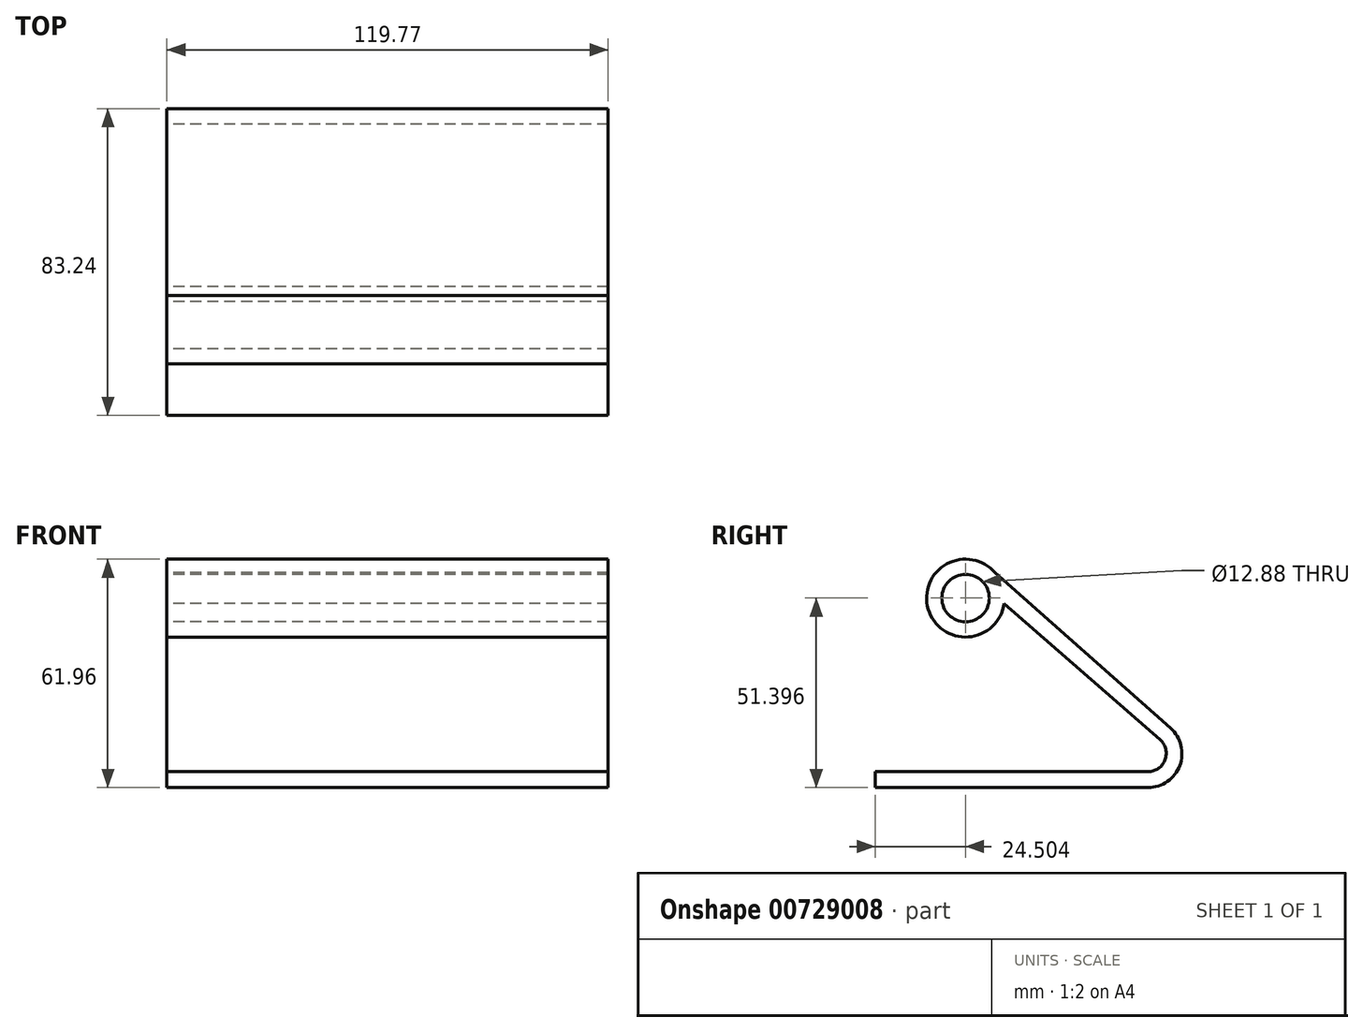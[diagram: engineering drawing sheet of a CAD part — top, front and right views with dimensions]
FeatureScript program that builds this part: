
annotation { "Feature Type Name" : "Feature", "Feature Type Description" : "" }
export const myFeature = defineFeature(function(context is Context, id is Id, definition is map)
    precondition{}
    {
        {
            var Q0;
            Q0=qCreatedBy(makeId("Right.planeOp"),FACE);
            var sketch = newSketch(context, id + "F0", { "sketchPlane" : qUnion([Q0])});
            skLineSegment(sketch, "E0", {"start": v(0, 0) * mm, "end": v(-39.98, 0) * mm});
            skLineSegment(sketch, "E1", {"start": v(-39.98, 0) * mm, "end": v(-39.98, 4.3) * mm});
            skLineSegment(sketch, "E2", {"start": v(-39.98, 4.3) * mm, "end": v(0, 4.3) * mm});
            skLineSegment(sketch, "E3", {"start": v(0, 4.3) * mm, "end": v(34.05, 4.3) * mm});
            skLineSegment(sketch, "E4", {"start": v(0, 0) * mm, "end": v(34.05, 0) * mm});
            skArc(sketch, "E5", {"start": v(34.05, 0) * mm, "mid": v(42.67, 5.95) * mm, "end": v(40.16, 16.12) * mm});
            skArc(sketch, "E6", {"start": v(34.05, 4.3) * mm, "mid": v(38.67, 7.5) * mm, "end": v(37.3, 12.95) * mm});
            skLineSegment(sketch, "E7", {"start": v(40.16, 16.12) * mm, "end": v(-7.47, 58.3) * mm});
            skLineSegment(sketch, "E8", {"start": v(37.3, 12.95) * mm, "end": v(-10.75, 54.96) * mm});
            skCircle(sketch, "E9", {"center": v(-15.48, 51.4) * mm, "radius": 10.57 * mm});
            skCircle(sketch, "E10", {"center": v(-15.48, 51.4) * mm, "radius": 6.44 * mm});
            skSolve(sketch);
        }
        {
            var Q0;
            Q0=makeQuery(id+"F0.imprint","IMPRINT",FACE,{"disambiguationData":[TD([[makeQuery(id+"F0.imprint","IMPRINT",EDGE,{"derivedFrom":sQuery(id+"F0.wireOp",EDGE,"E0")}),-1.0]])]});
            var Q1;
            Q1=makeQuery(id+"F0.imprint","IMPRINT",FACE,{"disambiguationData":[TD([[makeQuery(id+"F0.imprint","IMPRINT",EDGE,{"derivedFrom":sQuery(id+"F0.wireOp",EDGE,"E10")}),-1.0]])]});
            extrude(context, id + "F1", {"entities" : qUnion([Q0, Q1]), "depth" : 94.37 * mm, "offsetDistance" : 25.4 * mm});
        }
        {
            var Q0;
            Q0=makeQuery(id+"F1.opExtrude","CAP_FACE",FACE,{"disambiguationData":[OSD([sQuery(id+"F0.wireOp",EDGE,"E0"),sQuery(id+"F0.wireOp",EDGE,"E1"),sQuery(id+"F0.wireOp",EDGE,"E2"),sQuery(id+"F0.wireOp",EDGE,"E3"),sQuery(id+"F0.wireOp",EDGE,"E4"),sQuery(id+"F0.wireOp",EDGE,"E5"),sQuery(id+"F0.wireOp",EDGE,"E6"),sQuery(id+"F0.wireOp",EDGE,"E7"),sQuery(id+"F0.wireOp",EDGE,"E8"),sQuery(id+"F0.wireOp",EDGE,"E9"),sQuery(id+"F0.wireOp",EDGE,"E10")])],"isStart":true});
            extrude(context, id + "F2", {"entities" : qUnion([Q0]), "operationType" : NewBodyOperationType.ADD, "depth" : 25.4 * mm, "offsetDistance" : 25.4 * mm});
        }
    });
